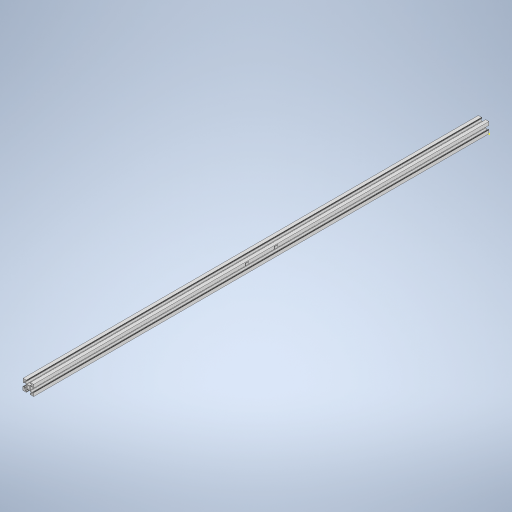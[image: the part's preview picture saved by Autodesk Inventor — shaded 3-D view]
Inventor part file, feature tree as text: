
AUTODESK INVENTOR PART (.ipt)
format: ipt  version: 2023.5 (Build 275446000, 446)  size: 427,520 bytes
history: native  units: in
note: dims shown in document units (in); Inventor stores cm internally (conversion verified against a paired STEP export)
features: sketch x5, extrude x4
ambient origin geometry x8: Origin, YZ Plane, XZ Plane, XY Plane, X Axis, Y Axis, Z Axis, Center Point
bodies: Solid1 (feature_tree)
feature tree (9):
  extrude  "Extrusion1"  Depth=33.94in TaperAngle=0.0deg
  extrude  "Extrusion2"  Depth=0.025in TaperAngle=0.0deg
  extrude  "Extrusion3"  Depth=0.2362in
  extrude  "Extrusion4"  Depth=0.025in TaperAngle=0.0deg
  sketch  "Sketch8"  dims[d77=1.0827in d78=1.0827in d79=0.1181in d80=0.2362in d81=0.1181in d82=0.2362in d83=0.025in d84=0.0in]
  sketch  "Sketch1"  dims[d59=0.05in d60=33.94in d61=0.0in]
  sketch  "Sketch5"  dims[d69=0.2362in d70=0.025in d71=0.0in]
  sketch  "Sketch6"  dims[d72=0.1181in d73=0.2362in]
  sketch  "Sketch7"  dims[d74=0.2362in d75=0.025in d76=0.0in]
